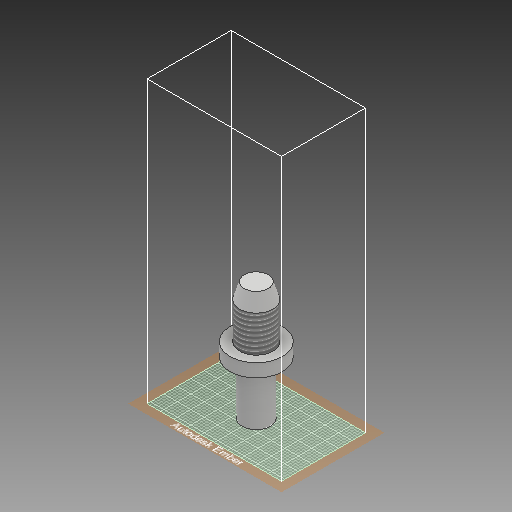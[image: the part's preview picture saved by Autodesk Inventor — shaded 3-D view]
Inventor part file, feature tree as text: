
AUTODESK INVENTOR PART (.ipt)
format: ipt  version: 2018 (Build 220112000, 112)  size: 606,720 bytes
history: native  units: in
note: dims shown in document units (in); Inventor stores cm internally (conversion verified against a paired STEP export)
features: sketch x8, extrude x3, plane x2, other x2, loft x1, helix x1
ambient origin geometry x8: Origin, YZ Plane, XZ Plane, XY Plane, X Axis, Y Axis, Z Axis, Center Point
bodies: Body1 (feature_tree)
feature tree (17):
  extrude  "Extrusion2"  Depth=0.2462in TaperAngle=0.0deg
  extrude  "Extrusion3"  Depth=1.0in TaperAngle=0.0deg
  extrude  "Extrusion4"  Depth=0.6821in TaperAngle=0.0deg
  plane  "Work Plane1"
  loft  "Loft1"
  sketch  "Sketch9"  dims[d23=0.05in d24=1.0in d25=5.315in d26=0.0in d27=90.0deg d28=90.0deg d29=0.0in d30=0.0in]
  other  "Work Axis1"
  sketch  "3D Sketch3"
  sketch  "3D Sketch4"
  plane  "Work Plane5"
  helix  "Coil1"  [1 undecoded]
  sketch  "Sketch3"  dims[d4=0.9781in d5=0.2462in d6=0.0in]
  sketch  "Sketch4"  dims[d7=0.5274in d8=1.0in d9=0.0in]
  sketch  "Sketch5"  dims[d10=0.6258in d11=0.6821in d12=0.0in]
  sketch  "Sketch7"  dims[d15=0.2899in d16=0.0in d17=90.0deg d18=0.0in d19=90.0deg]
  other  "Edges1"
  sketch  "Sketch14"
note: 1 required parameter value undecoded (feature->parameter linkage not recoverable at this tier; creation-order binding heuristic only, values carry confidence <= 0.55)
